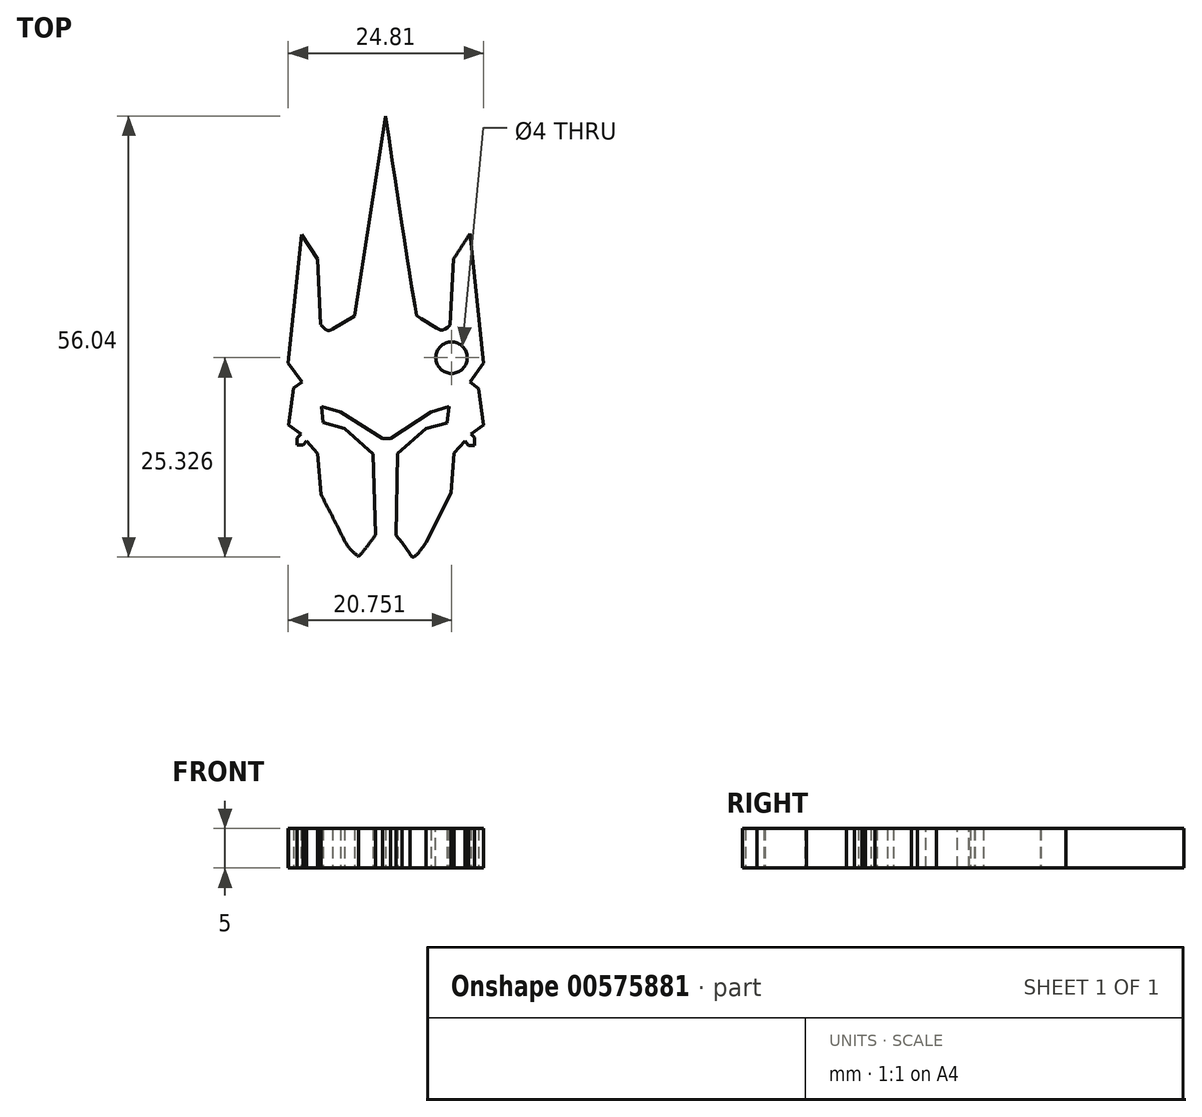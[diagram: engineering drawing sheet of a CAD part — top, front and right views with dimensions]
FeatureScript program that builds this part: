
annotation { "Feature Type Name" : "Feature", "Feature Type Description" : "" }
export const myFeature = defineFeature(function(context is Context, id is Id, definition is map)
    precondition{}
    {
        {
            var Q0;
            Q0=qCreatedBy(makeId("Top.planeOp"),FACE);
            var sketch = newSketch(context, id + "F0", { "sketchPlane" : qUnion([Q0])});
            skFitSpline(sketch, "E0", {"points": [v(29.97, 58.04) * mm, v(33.9, 32.8) * mm, v(34.11, 32.52) * mm, v(36.76, 30.92) * mm, v(37.34, 30.85) * mm, v(38.15, 31.47) * mm], "startDerivative": vector(9.68, -65) * mm, "endDerivative": vector(7.99, 7.08) * mm});
            skFitSpline(sketch, "E1", {"points": [v(38.15, 31.47) * mm, v(38.63, 39.9) * mm], "startDerivative": vector(0.48, 8.42) * mm, "endDerivative": vector(0.48, 8.42) * mm});
            skFitSpline(sketch, "E2", {"points": [v(38.63, 39.9) * mm, v(40.68, 43.1) * mm], "startDerivative": vector(2, 3.16) * mm, "endDerivative": vector(2, 3.16) * mm});
            skFitSpline(sketch, "E3", {"points": [v(40.68, 43.1) * mm, v(42.4, 26.62) * mm], "startDerivative": vector(1.72, -16.48) * mm, "endDerivative": vector(1.72, -16.48) * mm});
            skFitSpline(sketch, "E4", {"points": [v(42.4, 26.62) * mm, v(40.68, 24.23) * mm], "startDerivative": vector(-1.72, -2.4) * mm, "endDerivative": vector(-1.72, -2.4) * mm});
            skFitSpline(sketch, "E5", {"points": [v(40.68, 24.23) * mm, v(41.74, 23.44) * mm], "startDerivative": vector(1.06, -0.8) * mm, "endDerivative": vector(1.06, -0.8) * mm});
            skFitSpline(sketch, "E6", {"points": [v(41.74, 23.44) * mm, v(42.4, 18.8) * mm], "startDerivative": vector(0.66, -4.64) * mm, "endDerivative": vector(0.66, -4.64) * mm});
            skFitSpline(sketch, "E7", {"points": [v(42.4, 18.8) * mm, v(40.8, 17.64) * mm], "startDerivative": vector(-1.6, -1.16) * mm, "endDerivative": vector(-1.6, -1.16) * mm});
            skFitSpline(sketch, "E8", {"points": [v(40.8, 17.64) * mm, v(41.28, 17.18) * mm], "startDerivative": vector(0.53, -0.51) * mm, "endDerivative": vector(0.53, -0.51) * mm});
            skFitSpline(sketch, "E9", {"points": [v(41.28, 17.18) * mm, v(41.28, 16.2) * mm], "startDerivative": vector(0, -0.98) * mm, "endDerivative": vector(0, -0.98) * mm});
            skFitSpline(sketch, "E10", {"points": [v(41.28, 16.2) * mm, v(40.48, 16.2) * mm], "startDerivative": vector(-0.8, 0) * mm, "endDerivative": vector(-0.8, 0) * mm});
            skFitSpline(sketch, "E11", {"points": [v(40.48, 16.2) * mm, v(40.03, 16.76) * mm], "startDerivative": vector(-0.45, 0.56) * mm, "endDerivative": vector(-0.45, 0.56) * mm});
            skFitSpline(sketch, "E12", {"points": [v(40.03, 16.76) * mm, v(38.68, 15.24) * mm], "startDerivative": vector(-1.35, -1.52) * mm, "endDerivative": vector(-1.35, -1.52) * mm});
            skFitSpline(sketch, "E13", {"points": [v(38.68, 15.24) * mm, v(38.25, 10.13) * mm], "startDerivative": vector(-0.43, -5.1) * mm, "endDerivative": vector(-0.43, -5.1) * mm});
            skFitSpline(sketch, "E14", {"points": [v(38.25, 10.13) * mm, v(35.1, 3.83) * mm], "startDerivative": vector(-3.14, -6.3) * mm, "endDerivative": vector(-3.14, -6.3) * mm});
            skFitSpline(sketch, "E15", {"points": [v(35.1, 3.83) * mm, v(33.44, 2) * mm, v(33.05, 2.41) * mm], "startDerivative": vector(-2.9, -4.07) * mm, "endDerivative": vector(-0.99, 1.93) * mm});
            skFitSpline(sketch, "E16", {"points": [v(33.05, 2.41) * mm, v(32.04, 3.83) * mm], "startDerivative": vector(-1.02, 1.42) * mm, "endDerivative": vector(-1.02, 1.42) * mm});
            skFitSpline(sketch, "E17", {"points": [v(32.04, 3.83) * mm, v(31.28, 4.76) * mm], "startDerivative": vector(-0.75, 0.93) * mm, "endDerivative": vector(-0.75, 0.93) * mm});
            skFitSpline(sketch, "E18", {"points": [v(31.28, 4.76) * mm, v(31.48, 15.16) * mm], "startDerivative": vector(0.2, 10.4) * mm, "endDerivative": vector(0.2, 10.4) * mm});
            skFitSpline(sketch, "E19", {"points": [v(31.48, 15.16) * mm, v(35.1, 18.3) * mm], "startDerivative": vector(3.63, 3.14) * mm, "endDerivative": vector(3.63, 3.14) * mm});
            skFitSpline(sketch, "E20", {"points": [v(35.1, 18.3) * mm, v(37.79, 19.01) * mm], "startDerivative": vector(2.68, 0.71) * mm, "endDerivative": vector(2.68, 0.71) * mm});
            skFitSpline(sketch, "E21", {"points": [v(37.79, 19.01) * mm, v(38.04, 21.15) * mm], "startDerivative": vector(0.25, 2.14) * mm, "endDerivative": vector(0.25, 2.14) * mm});
            skFitSpline(sketch, "E22", {"points": [v(38.04, 21.15) * mm, v(35.73, 20.4) * mm], "startDerivative": vector(-2.3, -0.74) * mm, "endDerivative": vector(-2.3, -0.74) * mm});
            skFitSpline(sketch, "E23", {"points": [v(35.73, 20.4) * mm, v(30.58, 17.06) * mm], "startDerivative": vector(-5.15, -3.35) * mm, "endDerivative": vector(-5.15, -3.35) * mm});
            skFitSpline(sketch, "E24", {"points": [v(30.58, 17.06) * mm, v(29.57, 17.06) * mm], "startDerivative": vector(-1, 0) * mm, "endDerivative": vector(-1, 0) * mm});
            skFitSpline(sketch, "E25", {"points": [v(29.57, 17.06) * mm, v(24.24, 20.4) * mm], "startDerivative": vector(-5.34, 3.35) * mm, "endDerivative": vector(-5.34, 3.35) * mm});
            skFitSpline(sketch, "E26", {"points": [v(24.24, 20.4) * mm, v(21.85, 21.15) * mm], "startDerivative": vector(-2.39, 0.74) * mm, "endDerivative": vector(-2.39, 0.74) * mm});
            skFitSpline(sketch, "E27", {"points": [v(21.85, 21.15) * mm, v(22.03, 19.1) * mm], "startDerivative": vector(0.19, -2.05) * mm, "endDerivative": vector(0.19, -2.05) * mm});
            skFitSpline(sketch, "E28", {"points": [v(22.03, 19.1) * mm, v(24.77, 18.3) * mm], "startDerivative": vector(2.73, -0.8) * mm, "endDerivative": vector(2.73, -0.8) * mm});
            skFitSpline(sketch, "E29", {"points": [v(24.77, 18.3) * mm, v(28.4, 15.11) * mm], "startDerivative": vector(3.63, -3.19) * mm, "endDerivative": vector(3.63, -3.19) * mm});
            skFitSpline(sketch, "E30", {"points": [v(28.4, 15.11) * mm, v(28.67, 4.84) * mm], "startDerivative": vector(0.28, -10.27) * mm, "endDerivative": vector(0.28, -10.27) * mm});
            skFitSpline(sketch, "E31", {"points": [v(28.67, 4.8) * mm, v(28.67, 4.84) * mm], "startDerivative": vector(0, 0.04) * mm, "endDerivative": vector(0, 0.04) * mm});
            skFitSpline(sketch, "E32", {"points": [v(28.67, 4.8) * mm, v(26.55, 2.08) * mm], "startDerivative": vector(-1.88, -2.77) * mm, "endDerivative": vector(-2.35, -2.6) * mm});
            skFitSpline(sketch, "E33", {"points": [v(26.55, 2.08) * mm, v(25.38, 3.12) * mm, v(24.5, 4.6) * mm], "startDerivative": vector(-2.55, 1.95) * mm, "endDerivative": vector(-1.55, 3.08) * mm});
            skFitSpline(sketch, "E34", {"points": [v(24.5, 4.6) * mm, v(21.78, 9.94) * mm], "startDerivative": vector(-2.69, 5.3) * mm, "endDerivative": vector(-2.69, 5.3) * mm});
            skFitSpline(sketch, "E35", {"points": [v(21.78, 9.94) * mm, v(21.3, 15.16) * mm], "startDerivative": vector(-0.47, 5.22) * mm, "endDerivative": vector(-0.47, 5.22) * mm});
            skFitSpline(sketch, "E36", {"points": [v(21.3, 15.16) * mm, v(19.9, 16.74) * mm], "startDerivative": vector(-1.4, 1.59) * mm, "endDerivative": vector(-1.4, 1.59) * mm});
            skFitSpline(sketch, "E37", {"points": [v(19.9, 16.74) * mm, v(19.47, 16.23) * mm], "startDerivative": vector(-0.44, -0.5) * mm, "endDerivative": vector(-0.44, -0.5) * mm});
            skFitSpline(sketch, "E38", {"points": [v(19.47, 16.23) * mm, v(18.73, 16.23) * mm], "startDerivative": vector(-0.73, 0) * mm, "endDerivative": vector(-0.73, 0) * mm});
            skFitSpline(sketch, "E39", {"points": [v(18.73, 16.23) * mm, v(18.73, 17.13) * mm], "startDerivative": vector(0, 0.9) * mm, "endDerivative": vector(0, 0.9) * mm});
            skFitSpline(sketch, "E40", {"points": [v(18.73, 17.13) * mm, v(19.2, 17.6) * mm], "startDerivative": vector(0.48, 0.48) * mm, "endDerivative": vector(0.48, 0.48) * mm});
            skFitSpline(sketch, "E41", {"points": [v(19.2, 17.6) * mm, v(17.67, 18.78) * mm], "startDerivative": vector(-1.54, 1.17) * mm, "endDerivative": vector(-1.54, 1.17) * mm});
            skFitSpline(sketch, "E42", {"points": [v(17.67, 18.78) * mm, v(18.26, 23.48) * mm], "startDerivative": vector(0.6, 4.7) * mm, "endDerivative": vector(0.6, 4.7) * mm});
            skFitSpline(sketch, "E43", {"points": [v(18.26, 23.48) * mm, v(19.35, 24.22) * mm], "startDerivative": vector(1.1, 0.74) * mm, "endDerivative": vector(1.1, 0.74) * mm});
            skFitSpline(sketch, "E44", {"points": [v(19.35, 24.22) * mm, v(17.6, 26.67) * mm], "startDerivative": vector(-1.76, 2.45) * mm, "endDerivative": vector(-1.76, 2.45) * mm});
            skFitSpline(sketch, "E45", {"points": [v(17.6, 26.67) * mm, v(19.28, 42.98) * mm], "startDerivative": vector(1.69, 16.3) * mm, "endDerivative": vector(1.69, 16.3) * mm});
            skFitSpline(sketch, "E46", {"points": [v(19.28, 42.98) * mm, v(21.3, 39.83) * mm], "startDerivative": vector(2.01, -3.15) * mm, "endDerivative": vector(2.01, -3.15) * mm});
            skFitSpline(sketch, "E47", {"points": [v(21.3, 39.83) * mm, v(21.74, 31.52) * mm], "startDerivative": vector(0.45, -8.31) * mm, "endDerivative": vector(0.45, -8.31) * mm});
            skFitSpline(sketch, "E48", {"points": [v(21.74, 31.52) * mm, v(22.63, 30.8) * mm, v(23.23, 30.95) * mm], "startDerivative": vector(1.59, -1.73) * mm, "endDerivative": vector(1.4, 0.7) * mm});
            skFitSpline(sketch, "E49", {"points": [v(23.23, 30.95) * mm, v(26.04, 32.6) * mm], "startDerivative": vector(2.8, 1.66) * mm, "endDerivative": vector(2.8, 1.66) * mm});
            skFitSpline(sketch, "E50", {"points": [v(26.04, 32.6) * mm, v(29.97, 58.04) * mm], "startDerivative": vector(3.93, 25.44) * mm, "endDerivative": vector(3.93, 25.44) * mm});
            skSolve(sketch);
        }
        {
            var Q0;
            Q0 = qSketchRegion(id + "F0", true);
            extrude(context, id + "F1", {"entities" : qUnion([Q0]), "depth" : 5 * mm, "offsetDistance" : 25 * mm});
        }
        {
            var Q0;
            Q0=makeQuery(id+"F1.opExtrude","CAP_FACE",FACE,{"disambiguationData":[OSD([sQuery(id+"F0.wireOp",EDGE,"E0"),sQuery(id+"F0.wireOp",EDGE,"E1"),sQuery(id+"F0.wireOp",EDGE,"E2"),sQuery(id+"F0.wireOp",EDGE,"E3"),sQuery(id+"F0.wireOp",EDGE,"E4"),sQuery(id+"F0.wireOp",EDGE,"E5"),sQuery(id+"F0.wireOp",EDGE,"E6"),sQuery(id+"F0.wireOp",EDGE,"E7"),sQuery(id+"F0.wireOp",EDGE,"E8"),sQuery(id+"F0.wireOp",EDGE,"E9"),sQuery(id+"F0.wireOp",EDGE,"E10"),sQuery(id+"F0.wireOp",EDGE,"E11"),sQuery(id+"F0.wireOp",EDGE,"E12"),sQuery(id+"F0.wireOp",EDGE,"E13"),sQuery(id+"F0.wireOp",EDGE,"E14"),sQuery(id+"F0.wireOp",EDGE,"E15"),sQuery(id+"F0.wireOp",EDGE,"E16"),sQuery(id+"F0.wireOp",EDGE,"E17"),sQuery(id+"F0.wireOp",EDGE,"E18"),sQuery(id+"F0.wireOp",EDGE,"E19"),sQuery(id+"F0.wireOp",EDGE,"E20"),sQuery(id+"F0.wireOp",EDGE,"E21"),sQuery(id+"F0.wireOp",EDGE,"E22"),sQuery(id+"F0.wireOp",EDGE,"E23"),sQuery(id+"F0.wireOp",EDGE,"E24"),sQuery(id+"F0.wireOp",EDGE,"E25"),sQuery(id+"F0.wireOp",EDGE,"E26"),sQuery(id+"F0.wireOp",EDGE,"E27"),sQuery(id+"F0.wireOp",EDGE,"E28"),sQuery(id+"F0.wireOp",EDGE,"E29"),sQuery(id+"F0.wireOp",EDGE,"E30"),sQuery(id+"F0.wireOp",EDGE,"E31"),sQuery(id+"F0.wireOp",EDGE,"E32"),sQuery(id+"F0.wireOp",EDGE,"E33"),sQuery(id+"F0.wireOp",EDGE,"E34"),sQuery(id+"F0.wireOp",EDGE,"E35"),sQuery(id+"F0.wireOp",EDGE,"E36"),sQuery(id+"F0.wireOp",EDGE,"E37"),sQuery(id+"F0.wireOp",EDGE,"E38"),sQuery(id+"F0.wireOp",EDGE,"E39"),sQuery(id+"F0.wireOp",EDGE,"E40"),sQuery(id+"F0.wireOp",EDGE,"E41"),sQuery(id+"F0.wireOp",EDGE,"E42"),sQuery(id+"F0.wireOp",EDGE,"E43"),sQuery(id+"F0.wireOp",EDGE,"E44"),sQuery(id+"F0.wireOp",EDGE,"E45"),sQuery(id+"F0.wireOp",EDGE,"E46"),sQuery(id+"F0.wireOp",EDGE,"E47"),sQuery(id+"F0.wireOp",EDGE,"E48"),sQuery(id+"F0.wireOp",EDGE,"E49"),sQuery(id+"F0.wireOp",EDGE,"E50")])],"isStart":false});
            var sketch = newSketch(context, id + "F2", { "sketchPlane" : qUnion([Q0])});
            skCircle(sketch, "E51", {"center": v(38.34, 27.33) * mm, "radius": 2 * mm});
            skSolve(sketch);
        }
        {
            var Q0;
            Q0 = qSketchRegion(id + "F2", true);
            extrude(context, id + "F3", {"entities" : qUnion([Q0]), "operationType" : NewBodyOperationType.REMOVE, "oppositeDirection" : true, "depth" : 5 * mm, "offsetDistance" : 25 * mm});
        }
    });
